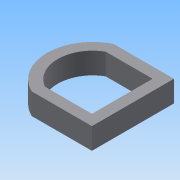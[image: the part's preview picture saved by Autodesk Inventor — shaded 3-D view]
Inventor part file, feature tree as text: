
AUTODESK INVENTOR PART (.ipt)
format: ipt  version: 2015 (Build 190159000, 159)  size: 99,328 bytes
history: native  units: in
note: dims shown in document units (in); Inventor stores cm internally (conversion verified against a paired STEP export)
features: extrude x1, sketch x1
ambient origin geometry x8: Origin, YZ Plane, XZ Plane, XY Plane, X Axis, Y Axis, Z Axis, Center Point
bodies: Body1 (feature_tree)
feature tree (2):
  extrude  "Extrusion2"  Depth=0.25in
  sketch  "Sketch1"  dims[d0=0.41in d1=0.55in d2=0.71in d3=0.573in d4=0.55in d5=0.71in d6=0.6in d7=0.55in d8=0.71in d10=0.55in d11=0.71in d13=0.125in d14=0.125in d15=0.125in d19=0.41in d20=0.125in d21=0.25in d22=0.0in]
